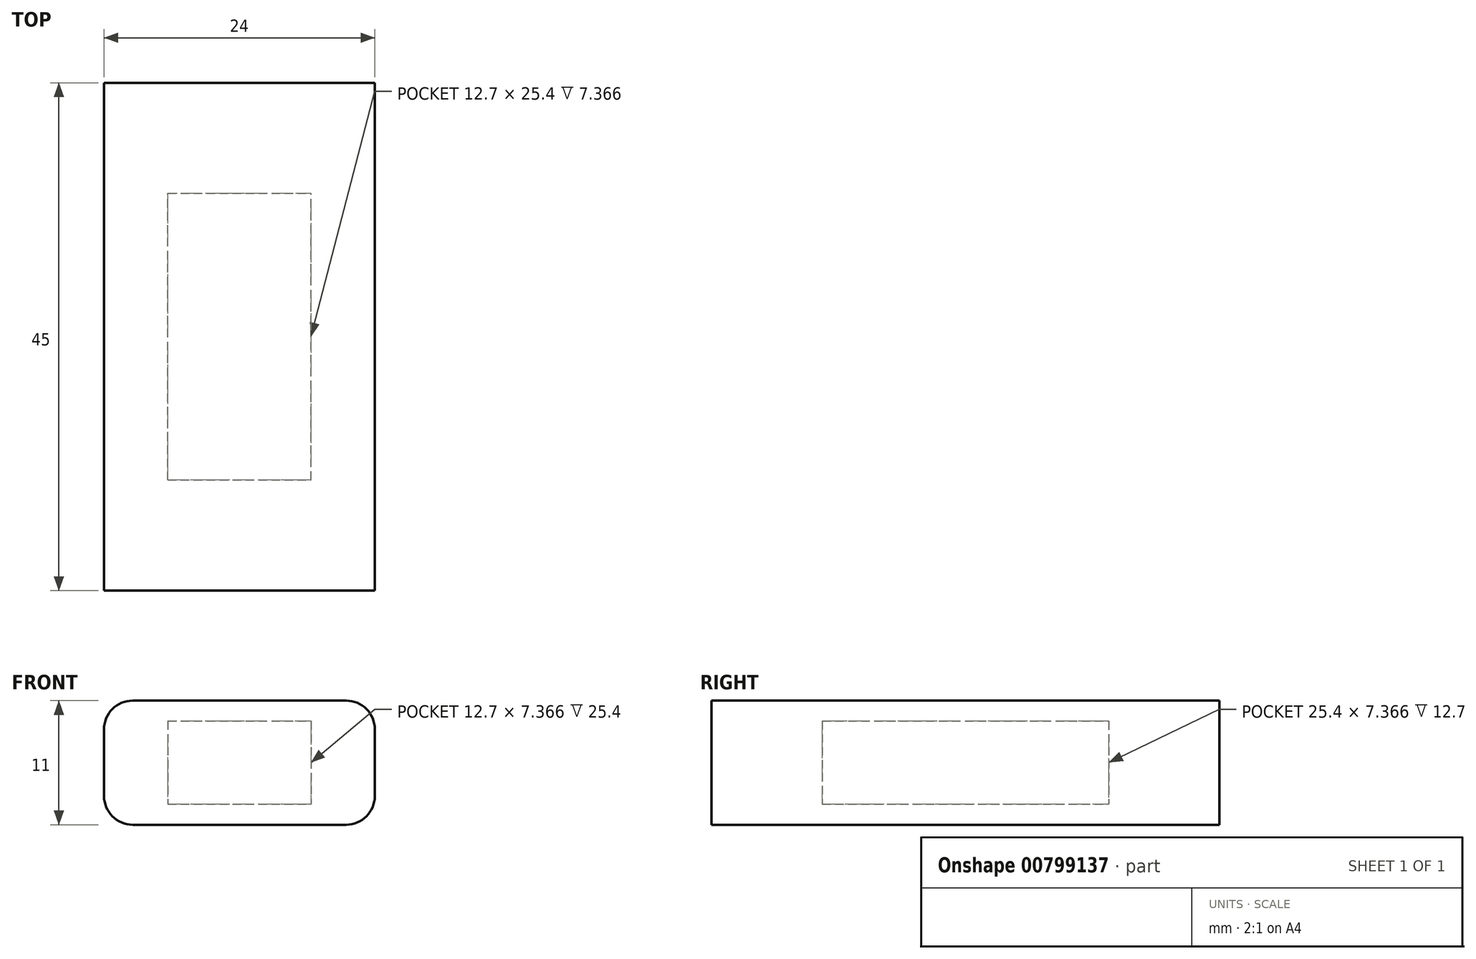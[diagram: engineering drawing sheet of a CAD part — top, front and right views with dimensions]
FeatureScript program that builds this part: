
annotation { "Feature Type Name" : "Feature", "Feature Type Description" : "" }
export const myFeature = defineFeature(function(context is Context, id is Id, definition is map)
    precondition{}
    {
        {
            var Q0;
            Q0=qCreatedBy(makeId("Front.planeOp"),FACE);
            var sketch = newSketch(context, id + "F0", { "sketchPlane" : qUnion([Q0])});
            skLineSegment(sketch, "E0.bottom", {"start": v(12, -5.5) * mm, "end": v(-12, -5.5) * mm});
            skLineSegment(sketch, "E0.top", {"start": v(12, 5.5) * mm, "end": v(-12, 5.5) * mm});
            skLineSegment(sketch, "E0.left", {"start": v(12, -5.5) * mm, "end": v(12, 5.5) * mm});
            skLineSegment(sketch, "E0.right", {"start": v(-12, -5.5) * mm, "end": v(-12, 5.5) * mm});
            skLineSegment(sketch, "E1", {"start": v(-12, -5.5) * mm, "end": v(12, 5.5) * mm, "construction": true});
            skPoint(sketch, "E2", {"position": v(0, 0) * mm});
            skSolve(sketch);
        }
        {
            var Q0;
            Q0 = qSketchRegion(id + "F0", true);
            extrude(context, id + "F1", {"entities" : qUnion([Q0]), "endBound" : BoundingType.SYMMETRIC, "depth" : 45 * mm, "offsetDistance" : 25.4 * mm});
        }
        {
            var Q0;
            Q0=makeQuery(id+"F1.opExtrude","SWEPT_EDGE",EDGE,{"disambiguationData":[OSD([sQuery(id+"F0.wireOp",EDGE,"E0.top"),sQuery(id+"F0.wireOp",EDGE,"E0.right")])]});
            var Q1;
            Q1=makeQuery(id+"F1.opExtrude","SWEPT_EDGE",EDGE,{"disambiguationData":[OSD([sQuery(id+"F0.wireOp",EDGE,"E0.bottom"),sQuery(id+"F0.wireOp",EDGE,"E0.right")])]});
            var Q2;
            Q2=makeQuery(id+"F1.opExtrude","SWEPT_EDGE",EDGE,{"disambiguationData":[OSD([sQuery(id+"F0.wireOp",EDGE,"E0.bottom"),sQuery(id+"F0.wireOp",EDGE,"E0.left")])]});
            var Q3;
            Q3=makeQuery(id+"F1.opExtrude","SWEPT_EDGE",EDGE,{"disambiguationData":[OSD([sQuery(id+"F0.wireOp",EDGE,"E0.top"),sQuery(id+"F0.wireOp",EDGE,"E0.left")])]});
            fillet(context, id + "F2", {"entities" : qUnion([Q0, Q1, Q2, Q3]), "radius" : 2.54 * mm, "tangentPropagation" : true, "allowEdgeOverflow" : false});
        }
        {
            var Q0;
            Q0=qCreatedBy(makeId("Top.planeOp"),FACE);
            var sketch = newSketch(context, id + "F3", { "sketchPlane" : qUnion([Q0])});
            skLineSegment(sketch, "E3.bottom", {"start": v(-6.35, -12.7) * mm, "end": v(6.35, -12.7) * mm});
            skLineSegment(sketch, "E3.top", {"start": v(-6.35, 12.7) * mm, "end": v(6.35, 12.7) * mm});
            skLineSegment(sketch, "E3.left", {"start": v(-6.35, -12.7) * mm, "end": v(-6.35, 12.7) * mm});
            skLineSegment(sketch, "E3.right", {"start": v(6.35, -12.7) * mm, "end": v(6.35, 12.7) * mm});
            skLineSegment(sketch, "E4", {"start": v(-6.35, -12.7) * mm, "end": v(6.35, 12.7) * mm, "construction": true});
            skPoint(sketch, "E5", {"position": v(0, 0) * mm});
            skSolve(sketch);
        }
        {
            var Q0;
            Q0 = qSketchRegion(id + "F3", true);
            extrude(context, id + "F4", {"entities" : qUnion([Q0]), "operationType" : NewBodyOperationType.REMOVE, "endBound" : BoundingType.SYMMETRIC, "depth" : 7.37 * mm, "offsetDistance" : 25.4 * mm});
        }
    });
